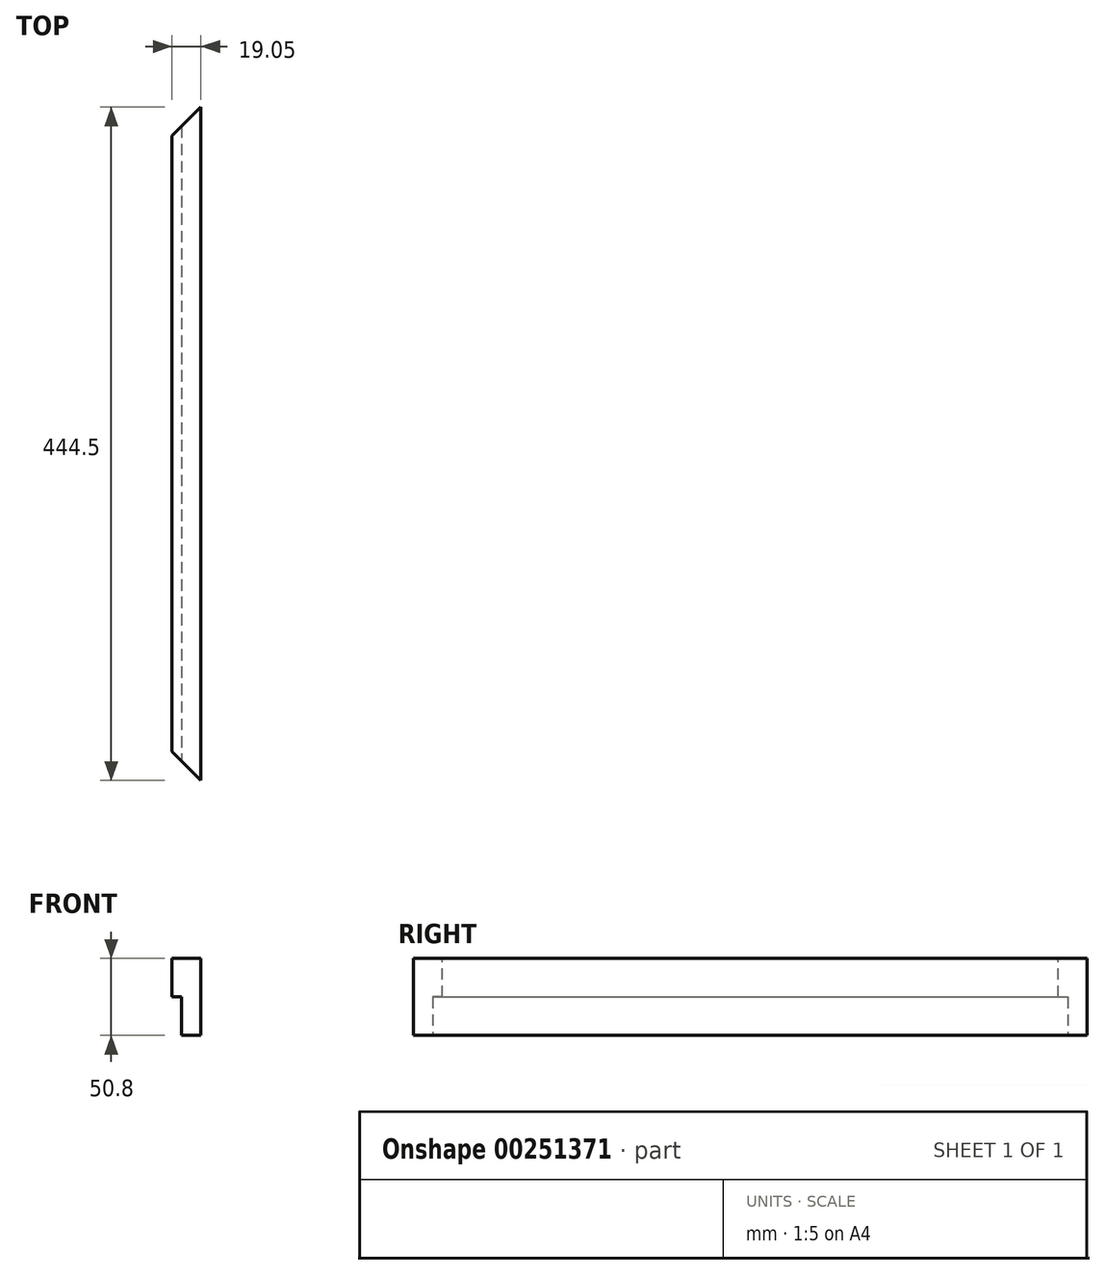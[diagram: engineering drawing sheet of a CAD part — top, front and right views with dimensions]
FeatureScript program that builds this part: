
annotation { "Feature Type Name" : "Feature", "Feature Type Description" : "" }
export const myFeature = defineFeature(function(context is Context, id is Id, definition is map)
    precondition{}
    {
        {
            var Q0;
            Q0=qCreatedBy(makeId("Right.planeOp"),FACE);
            var sketch = newSketch(context, id + "F0", { "sketchPlane" : qUnion([Q0])});
            skLineSegment(sketch, "E0.bottom", {"start": v(-184.15, 25.4) * mm, "end": v(184.15, 25.4) * mm});
            skLineSegment(sketch, "E0.top", {"start": v(-184.15, -25.4) * mm, "end": v(184.15, -25.4) * mm});
            skLineSegment(sketch, "E0.left", {"start": v(-184.15, 25.4) * mm, "end": v(-184.15, -25.4) * mm});
            skLineSegment(sketch, "E0.right", {"start": v(184.15, 25.4) * mm, "end": v(184.15, -25.4) * mm});
            skPoint(sketch, "E0.middle", {"position": v(0, 0) * mm});
            skSolve(sketch);
        }
        {
            var Q0;
            Q0 = qSketchRegion(id + "F0", true);
            extrude(context, id + "F1", {"entities" : qUnion([Q0]), "depth" : 19.05 * mm});
        }
        {
            var Q0;
            Q0=makeQuery(id+"F1.opExtrude","SWEPT_FACE",FACE,{"disambiguationData":[OSD([sQuery(id+"F0.wireOp",EDGE,"E0.left")])]});
            extrude(context, id + "F2", {"entities" : qUnion([Q0]), "operationType" : NewBodyOperationType.ADD, "depth" : 50.8 * mm});
        }
        {
            var Q0;
            Q0=makeQuery(id+"F1.opExtrude","SWEPT_FACE",FACE,{"disambiguationData":[OSD([sQuery(id+"F0.wireOp",EDGE,"E0.right")])]});
            extrude(context, id + "F3", {"entities" : qUnion([Q0]), "operationType" : NewBodyOperationType.ADD, "depth" : 25.4 * mm});
        }
        {
            var Q0;
            Q0=makeQuery(id+"F3.opExtrude","CAP_FACE",FACE,{"disambiguationData":[OSD([sQuery(id+"F0.wireOp",EDGE,"E0.right")])],"isStart":false});
            var sketch = newSketch(context, id + "F4", { "sketchPlane" : qUnion([Q0])});
            skLineSegment(sketch, "E1", {"start": v(-19.05, -25.4) * mm, "end": v(-6.35, -25.4) * mm});
            skLineSegment(sketch, "E2", {"start": v(-6.35, -25.4) * mm, "end": v(-6.35, 0) * mm});
            skLineSegment(sketch, "E3", {"start": v(-6.35, 0) * mm, "end": v(8.15, 0) * mm});
            skLineSegment(sketch, "E4", {"start": v(8.15, 0) * mm, "end": v(8.15, -26.95) * mm});
            skLineSegment(sketch, "E5", {"start": v(8.15, -26.95) * mm, "end": v(-6.35, -26.95) * mm});
            skLineSegment(sketch, "E6", {"start": v(-6.35, -26.95) * mm, "end": v(-6.35, -25.4) * mm});
            skSolve(sketch);
        }
        {
            var Q0;
            Q0 = qSketchRegion(id + "F4", true);
            extrude(context, id + "F5", {"entities" : qUnion([Q0]), "operationType" : NewBodyOperationType.REMOVE, "endBound" : BoundingType.THROUGH_ALL, "oppositeDirection" : true, "depth" : 25.4 * mm});
        }
        {
            var Q0;
            {var subQ0=sQuery(id+"F0.wireOp",EDGE,"E0.bottom");Q0=makeQuery(id+"F3.boolean.opBoolean","MERGE",FACE,{"derivedFrom":[makeQuery(id+"F2.boolean.opBoolean","MERGE",FACE,{"derivedFrom":[makeQuery(id+"F1.opExtrude","SWEPT_FACE",FACE,{"disambiguationData":[OSD([subQ0])]}),makeQuery(id+"F2.opExtrude","SWEPT_FACE",FACE,{"disambiguationData":[OSD([subQ0,sQuery(id+"F0.wireOp",EDGE,"E0.left")])]})]}),makeQuery(id+"F3.opExtrude","SWEPT_FACE",FACE,{"disambiguationData":[OSD([subQ0,sQuery(id+"F0.wireOp",EDGE,"E0.right")])]})]});}
            var sketch = newSketch(context, id + "F6", { "sketchPlane" : qUnion([Q0])});
            skLineSegment(sketch, "E7", {"start": v(19.05, 209.55) * mm, "end": v(0, 190.5) * mm});
            skLineSegment(sketch, "E8", {"start": v(0, 190.5) * mm, "end": v(-11.84, 190.5) * mm});
            skLineSegment(sketch, "E9", {"start": v(-11.84, 190.5) * mm, "end": v(-11.84, 224.02) * mm});
            skLineSegment(sketch, "E10", {"start": v(-11.84, 224.02) * mm, "end": v(19.28, 224.02) * mm});
            skLineSegment(sketch, "E11", {"start": v(19.28, 224.02) * mm, "end": v(19.05, 209.55) * mm});
            skLineSegment(sketch, "E12", {"start": v(19.05, -234.95) * mm, "end": v(0, -215.9) * mm});
            skLineSegment(sketch, "E13", {"start": v(0, -215.9) * mm, "end": v(-3.5, -215.9) * mm});
            skLineSegment(sketch, "E14", {"start": v(-3.5, -215.9) * mm, "end": v(-3.5, -242.68) * mm});
            skLineSegment(sketch, "E15", {"start": v(-3.5, -242.68) * mm, "end": v(19.05, -242.68) * mm});
            skLineSegment(sketch, "E16", {"start": v(19.05, -242.68) * mm, "end": v(19.05, -234.95) * mm});
            skSolve(sketch);
        }
        {
            var Q0;
            Q0 = qSketchRegion(id + "F6", true);
            extrude(context, id + "F7", {"entities" : qUnion([Q0]), "operationType" : NewBodyOperationType.REMOVE, "endBound" : BoundingType.THROUGH_ALL, "oppositeDirection" : true, "depth" : 25.4 * mm});
        }
    });
